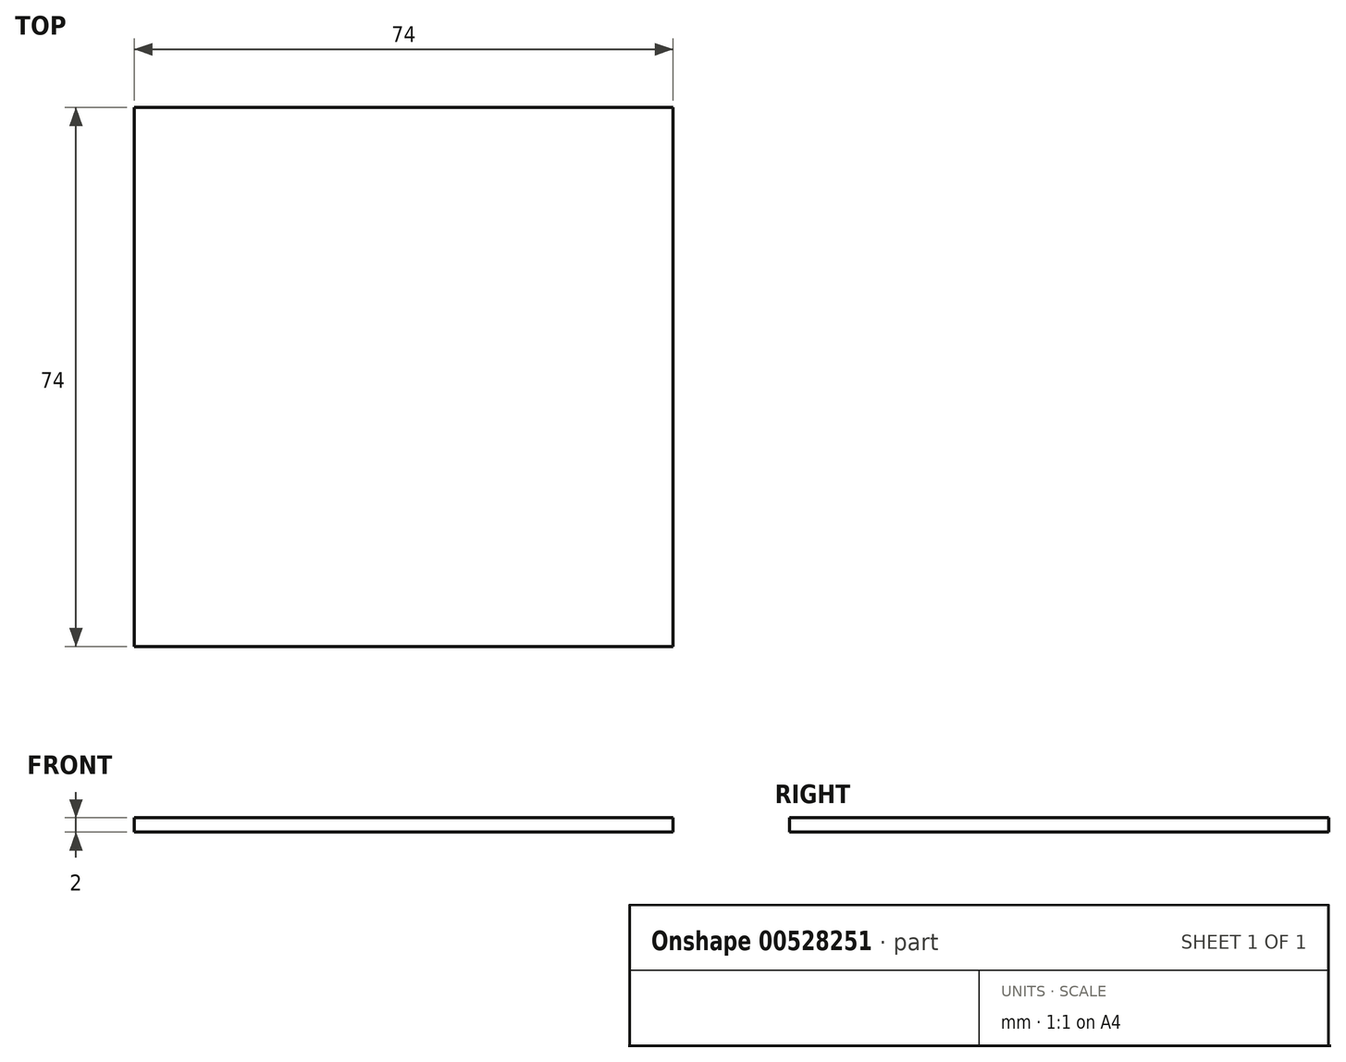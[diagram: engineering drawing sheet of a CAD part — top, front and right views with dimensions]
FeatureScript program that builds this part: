
annotation { "Feature Type Name" : "Feature", "Feature Type Description" : "" }
export const myFeature = defineFeature(function(context is Context, id is Id, definition is map)
    precondition{}
    {
        {
            var Q0;
            Q0=qCreatedBy(makeId("Top.planeOp"),FACE);
            var sketch = newSketch(context, id + "F0", { "sketchPlane" : qUnion([Q0])});
            skLineSegment(sketch, "E0.bottom", {"start": v(0, 0) * mm, "end": v(74, 0) * mm});
            skLineSegment(sketch, "E0.top", {"start": v(0, 74) * mm, "end": v(74, 74) * mm});
            skLineSegment(sketch, "E0.left", {"start": v(0, 0) * mm, "end": v(0, 74) * mm});
            skLineSegment(sketch, "E0.right", {"start": v(74, 0) * mm, "end": v(74, 74) * mm});
            skSolve(sketch);
        }
        {
            var Q0;
            Q0 = qSketchRegion(id + "F0", true);
            extrude(context, id + "F1", {"entities" : qUnion([Q0]), "depth" : 2 * mm, "offsetDistance" : 25 * mm});
        }
    });
